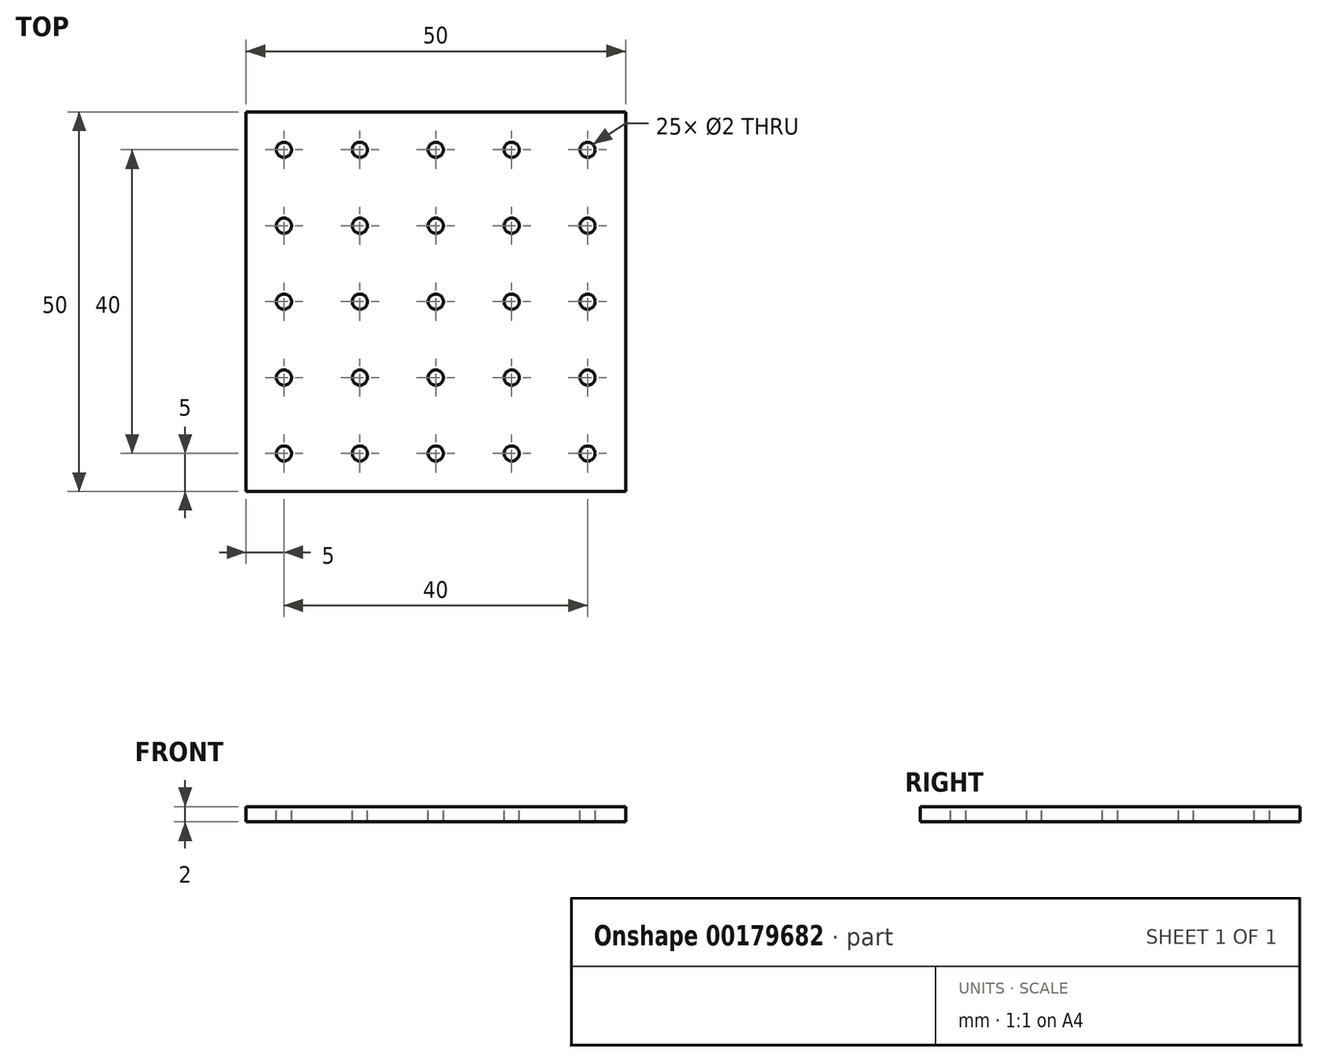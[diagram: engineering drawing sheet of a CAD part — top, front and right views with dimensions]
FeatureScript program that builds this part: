
annotation { "Feature Type Name" : "Feature", "Feature Type Description" : "" }
export const myFeature = defineFeature(function(context is Context, id is Id, definition is map)
    precondition{}
    {
        {
            var Q0;
            Q0=qCreatedBy(makeId("Top.planeOp"),FACE);
            var sketch = newSketch(context, id + "F0", { "sketchPlane" : qUnion([Q0])});
            skLineSegment(sketch, "E0.bottom", {"start": v(0, 0) * mm, "end": v(50, 0) * mm});
            skLineSegment(sketch, "E0.top", {"start": v(0, 50) * mm, "end": v(50, 50) * mm});
            skLineSegment(sketch, "E0.left", {"start": v(0, 0) * mm, "end": v(0, 50) * mm});
            skLineSegment(sketch, "E0.right", {"start": v(50, 0) * mm, "end": v(50, 50) * mm});
            skSolve(sketch);
        }
        {
            var Q0;
            Q0 = qSketchRegion(id + "F0", true);
            extrude(context, id + "F1", {"entities" : qUnion([Q0]), "depth" : 2 * mm});
        }
        {
            var Q0;
            Q0=makeQuery(id+"F1.opExtrude","CAP_FACE",FACE,{"disambiguationData":[OSD([sQuery(id+"F0.wireOp",EDGE,"E0.bottom"),sQuery(id+"F0.wireOp",EDGE,"E0.top"),sQuery(id+"F0.wireOp",EDGE,"E0.left"),sQuery(id+"F0.wireOp",EDGE,"E0.right")])],"isStart":false});
            var sketch = newSketch(context, id + "F2", { "sketchPlane" : qUnion([Q0])});
            skCircle(sketch, "E1", {"center": v(5, 5) * mm, "radius": 1 * mm});
            skLineSegment(sketch, "E2", {"start": v(0, 5) * mm, "end": v(5, 5) * mm});
            skLineSegment(sketch, "E3", {"start": v(5, 5) * mm, "end": v(5, 0) * mm});
            skLineSegment(sketch, "E4", {"start": v(50, 5) * mm, "end": v(45, 5) * mm});
            skLineSegment(sketch, "E5", {"start": v(45, 5) * mm, "end": v(45, 0) * mm});
            skCircle(sketch, "E6.0.1.0", {"center": v(5, 15) * mm, "radius": 1 * mm});
            skCircle(sketch, "E6.0.2.0", {"center": v(5, 25) * mm, "radius": 1 * mm});
            skCircle(sketch, "E6.0.3.0", {"center": v(5, 35) * mm, "radius": 1 * mm});
            skCircle(sketch, "E6.0.4.0", {"center": v(5, 45) * mm, "radius": 1 * mm});
            skCircle(sketch, "E6.1.0.0", {"center": v(15, 5) * mm, "radius": 1 * mm});
            skCircle(sketch, "E6.1.1.0", {"center": v(15, 15) * mm, "radius": 1 * mm});
            skCircle(sketch, "E6.1.2.0", {"center": v(15, 25) * mm, "radius": 1 * mm});
            skCircle(sketch, "E6.1.3.0", {"center": v(15, 35) * mm, "radius": 1 * mm});
            skCircle(sketch, "E6.1.4.0", {"center": v(15, 45) * mm, "radius": 1 * mm});
            skCircle(sketch, "E6.2.0.0", {"center": v(25, 5) * mm, "radius": 1 * mm});
            skCircle(sketch, "E6.2.1.0", {"center": v(25, 15) * mm, "radius": 1 * mm});
            skCircle(sketch, "E6.2.2.0", {"center": v(25, 25) * mm, "radius": 1 * mm});
            skCircle(sketch, "E6.2.3.0", {"center": v(25, 35) * mm, "radius": 1 * mm});
            skCircle(sketch, "E6.2.4.0", {"center": v(25, 45) * mm, "radius": 1 * mm});
            skCircle(sketch, "E6.3.0.0", {"center": v(35, 5) * mm, "radius": 1 * mm});
            skCircle(sketch, "E6.3.1.0", {"center": v(35, 15) * mm, "radius": 1 * mm});
            skCircle(sketch, "E6.3.2.0", {"center": v(35, 25) * mm, "radius": 1 * mm});
            skCircle(sketch, "E6.3.3.0", {"center": v(35, 35) * mm, "radius": 1 * mm});
            skCircle(sketch, "E6.3.4.0", {"center": v(35, 45) * mm, "radius": 1 * mm});
            skCircle(sketch, "E6.4.0.0", {"center": v(45, 5) * mm, "radius": 1 * mm});
            skCircle(sketch, "E6.4.1.0", {"center": v(45, 15) * mm, "radius": 1 * mm});
            skCircle(sketch, "E6.4.2.0", {"center": v(45, 25) * mm, "radius": 1 * mm});
            skCircle(sketch, "E6.4.3.0", {"center": v(45, 35) * mm, "radius": 1 * mm});
            skCircle(sketch, "E6.4.4.0", {"center": v(45, 45) * mm, "radius": 1 * mm});
            skLineSegment(sketch, "E6.direction1", {"start": v(5, 5) * mm, "end": v(15, 5) * mm, "construction": true});
            skLineSegment(sketch, "E6.direction2", {"start": v(5, 5) * mm, "end": v(5, 15) * mm, "construction": true});
            skSolve(sketch);
        }
        {
            var Q0;
            Q0 = qSketchRegion(id + "F2", true);
            extrude(context, id + "F3", {"entities" : qUnion([Q0]), "operationType" : NewBodyOperationType.REMOVE, "oppositeDirection" : true, "depth" : 25 * mm});
        }
    });
